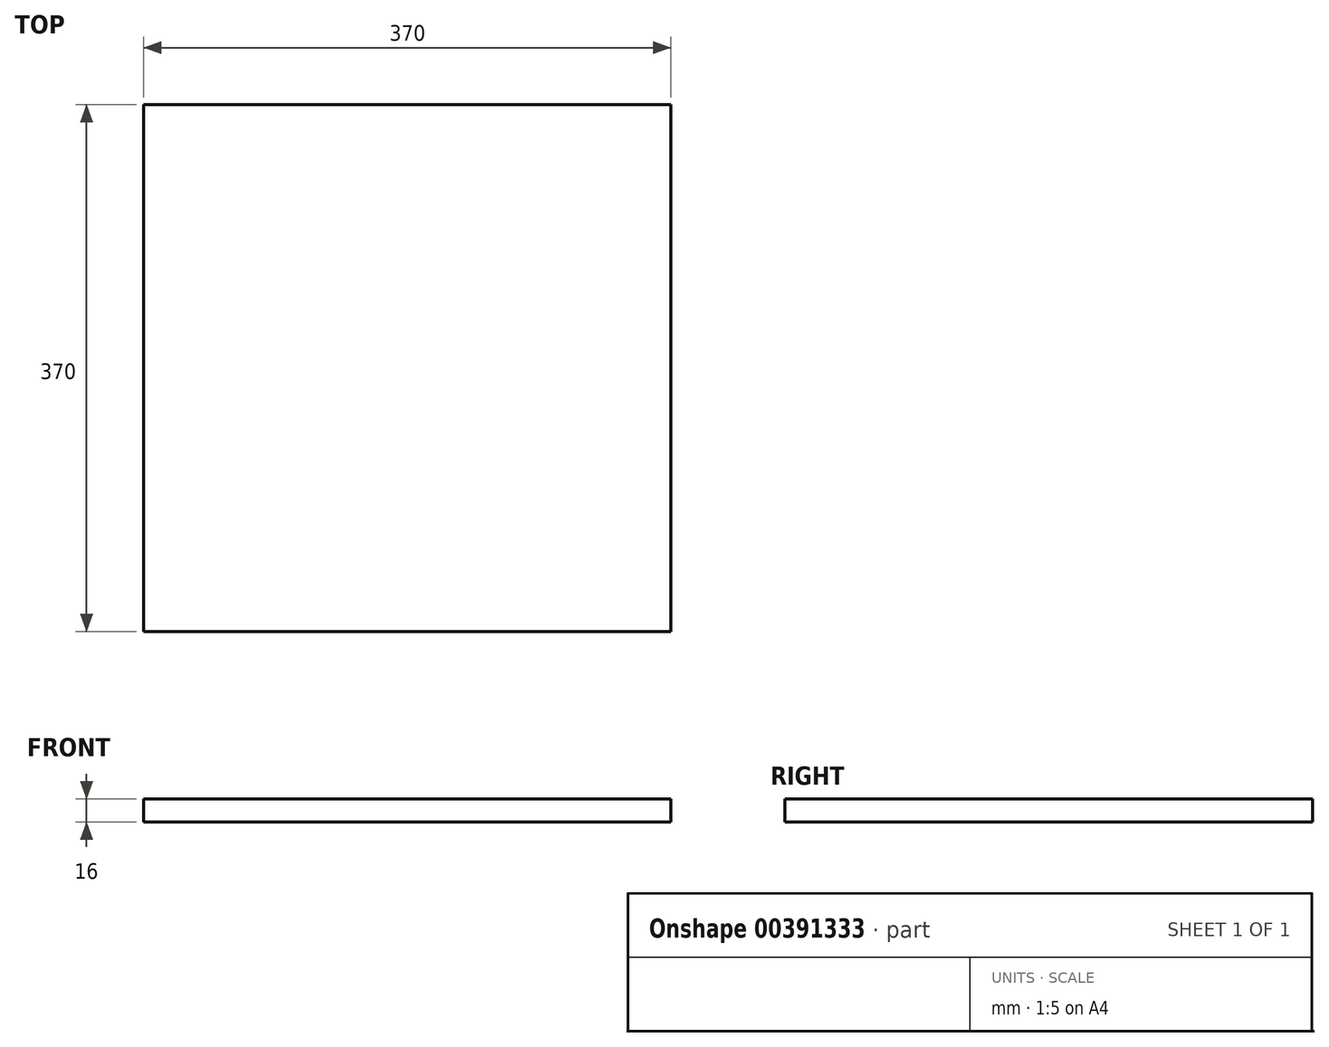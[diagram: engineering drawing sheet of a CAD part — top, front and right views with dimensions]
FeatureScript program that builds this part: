
annotation { "Feature Type Name" : "Feature", "Feature Type Description" : "" }
export const myFeature = defineFeature(function(context is Context, id is Id, definition is map)
    precondition{}
    {
        {
            var Q0;
            Q0=qCreatedBy(makeId("Top.planeOp"),FACE);
            var sketch = newSketch(context, id + "F0", { "sketchPlane" : qUnion([Q0])});
            skLineSegment(sketch, "E0.bottom", {"start": v(-185, 185) * mm, "end": v(185, 185) * mm});
            skLineSegment(sketch, "E0.top", {"start": v(-185, -185) * mm, "end": v(185, -185) * mm});
            skLineSegment(sketch, "E0.left", {"start": v(-185, 185) * mm, "end": v(-185, -185) * mm});
            skLineSegment(sketch, "E0.right", {"start": v(185, 185) * mm, "end": v(185, -185) * mm});
            skSolve(sketch);
        }
        {
            var Q0;
            Q0=makeQuery(id+"F0.imprint","IMPRINT",FACE,{"disambiguationData":[TD([[makeQuery(id+"F0.imprint","IMPRINT",EDGE,{"derivedFrom":sQuery(id+"F0.wireOp",EDGE,"E0.bottom")}),-1.0]])]});
            extrude(context, id + "F1", {"entities" : qUnion([Q0]), "depth" : 16 * mm});
        }
    });
